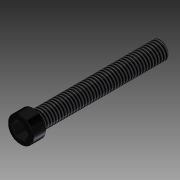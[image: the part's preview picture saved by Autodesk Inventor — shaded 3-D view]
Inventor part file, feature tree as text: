
AUTODESK INVENTOR PART (.ipt)
format: ipt  version: 2013 (Build 170138000, 138)  size: 109,056 bytes
history: native  units: in
note: dims shown in document units (in); Inventor stores cm internally (conversion verified against a paired STEP export)
features: extrude x3, sketch x1, thread x1, chamfer x1
ambient origin geometry x8: Origin, YZ Plane, XZ Plane, XY Plane, X Axis, Y Axis, Z Axis, Center Point
bodies: Solid1 (feature_tree)
feature tree (6):
  sketch  "Sketch1"  dims[d0=0.275in d1=0.185in d2=0.15in d3=0.15in d4=0.0in d5=1.35in d6=0.0in d7=0.05in d8=0.0in d9=1.0in d10=0.0in d11=0.01in d12=0.125in d13=45.0deg]
  extrude  "Extrusion1"  Depth=0.185in
  extrude  "Extrusion2"  Depth=0.15in
  extrude  "Extrusion3"  Depth=0.15in TaperAngle=0.0deg
  thread  "Thread1"  [1 undecoded]
  chamfer  "Chamfer1"  Distance=0.05in
note: 1 required parameter value undecoded (feature->parameter linkage not recoverable at this tier; creation-order binding heuristic only, values carry confidence <= 0.55)
